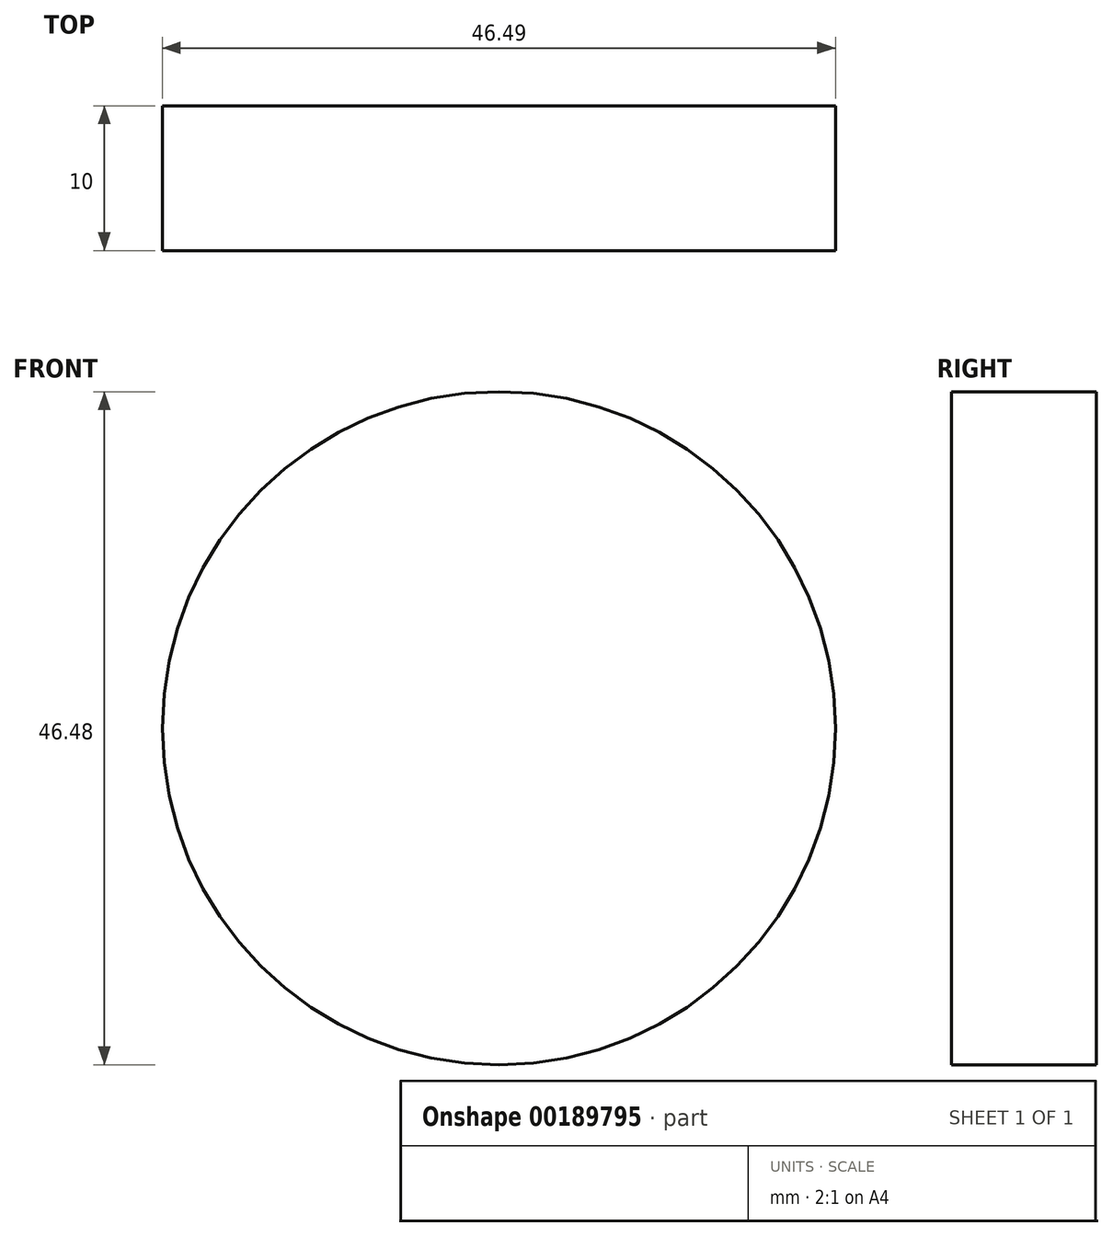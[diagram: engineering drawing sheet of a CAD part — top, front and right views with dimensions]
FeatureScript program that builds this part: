
annotation { "Feature Type Name" : "Feature", "Feature Type Description" : "" }
export const myFeature = defineFeature(function(context is Context, id is Id, definition is map)
    precondition{}
    {
        {
            var Q0;
            Q0=qCreatedBy(makeId("Front.planeOp"),FACE);
            var sketch = newSketch(context, id + "F0", { "sketchPlane" : qUnion([Q0])});
            skCircle(sketch, "E0", {"center": v(1.77, 0) * mm, "radius": 23.24 * mm});
            skSolve(sketch);
        }
        {
            var Q0;
            Q0=makeQuery(id+"F0.imprint","IMPRINT",FACE,{"disambiguationData":[TD([[makeQuery(id+"F0.imprint","IMPRINT",EDGE,{"derivedFrom":sQuery(id+"F0.wireOp",EDGE,"E0")}),1.0]])]});
            extrude(context, id + "F1", {"entities" : qUnion([Q0]), "depth" : 10 * mm});
        }
    });
